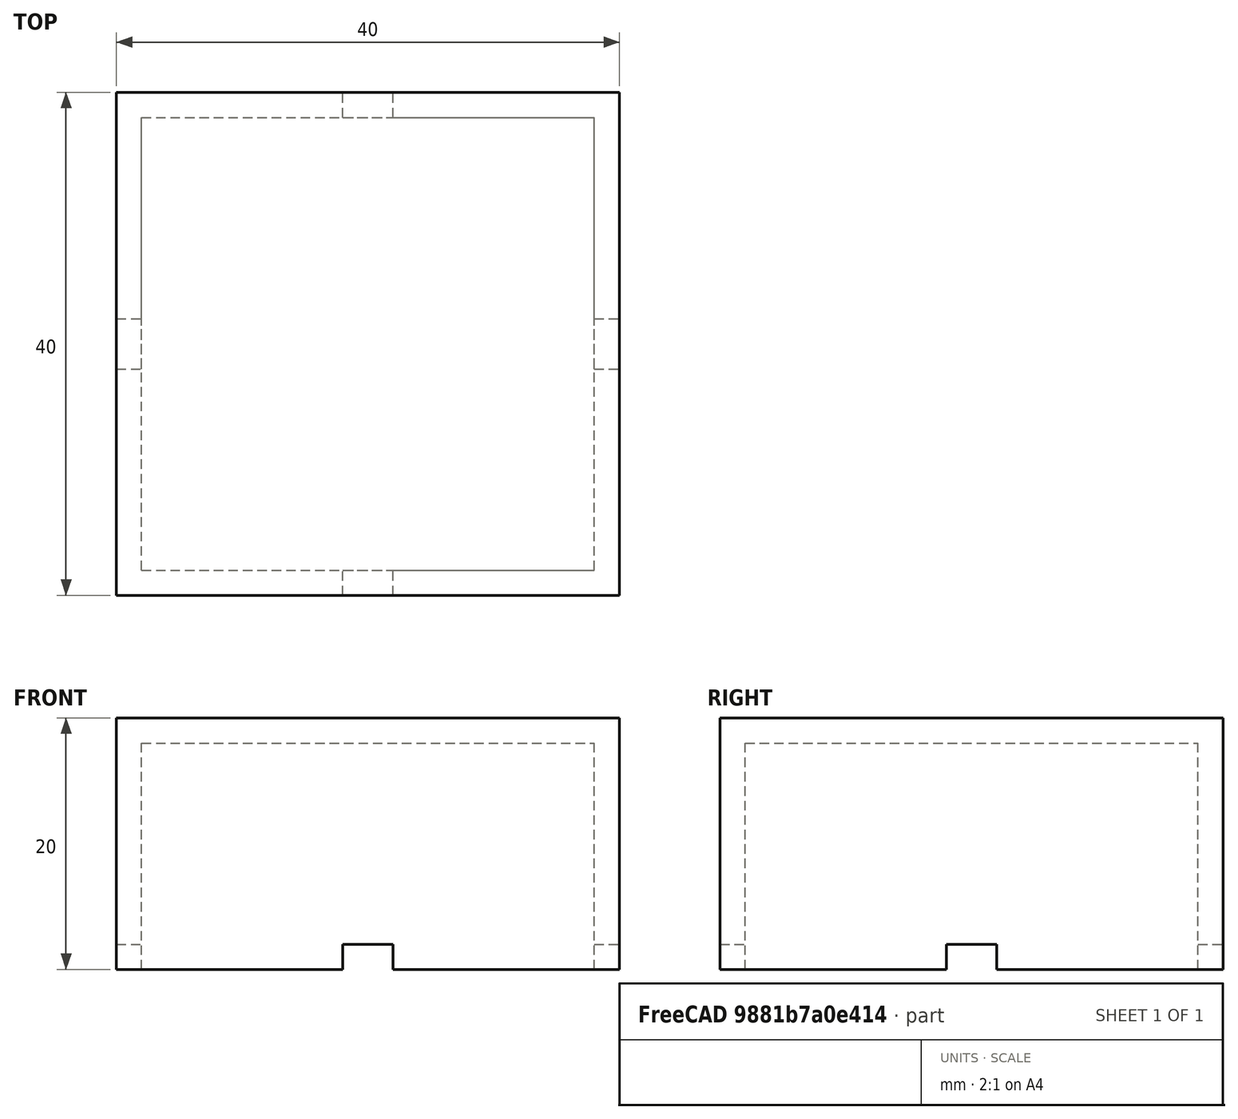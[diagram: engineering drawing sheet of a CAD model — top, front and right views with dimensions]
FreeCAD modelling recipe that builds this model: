
FCSTD DOCUMENT  (FreeCAD 0.16R6702 (Git))
Label: Untitled
License: All rights reserved
LicenseURL: http://en.wikipedia.org/wiki/All_rights_reserved
objects: Part::Box×6, Part::Cut×5
note: 11 computed .brp shape members not serialized (recipe doc carries the construction recipe); baked Part::Feature solids carry a one-line shape summary decoded from their .brp

FEATURE [Part::Box] Box  label="Cubo"
  Height = 20
  Length = 40
  Width = 40
FEATURE [Part::Box] Box001  label="Cubo001"
  Height = 18
  Length = 36
  Placement = pos=(2,2,0) rot=(0,0,1;0rad)
  Width = 36
FEATURE [Part::Cut] Cut
  Base = -> Box
  Tool = -> Box001
FEATURE [Part::Box] Box002  label="Cubo002"
  Height = 2
  Length = 2
  Placement = pos=(0,18,0) rot=(0,0,1;0rad)
  Width = 4
FEATURE [Part::Cut] Cut001
  Base = -> Cut
  Tool = -> Box002
FEATURE [Part::Box] Box003  label="Cubo003"
  Height = 2
  Length = 4
  Placement = pos=(18,0,0) rot=(0,0,1;0rad)
  Width = 2
FEATURE [Part::Cut] Cut002
  Base = -> Cut001
  Tool = -> Box003
FEATURE [Part::Box] Box004  label="Cubo004"
  Height = 2
  Length = 2
  Placement = pos=(38,18,0) rot=(0,0,1;0rad)
  Width = 4
FEATURE [Part::Cut] Cut003
  Base = -> Cut002
  Tool = -> Box004
FEATURE [Part::Box] Box005  label="Cubo005"
  Height = 2
  Length = 4
  Placement = pos=(18,38,0) rot=(0,0,1;0rad)
  Width = 2
FEATURE [Part::Cut] Cut004
  Base = -> Cut003
  Tool = -> Box005
